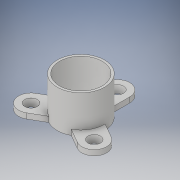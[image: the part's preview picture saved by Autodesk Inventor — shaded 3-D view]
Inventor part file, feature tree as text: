
AUTODESK INVENTOR PART (.ipt)
format: ipt  version: 2018 (Build 220112000, 112)  size: 190,976 bytes
history: native  units: in
note: dims shown in document units (in); Inventor stores cm internally (conversion verified against a paired STEP export)
features: sketch x5, extrude x4, plane x3, revolve x3, other x2, projected_geometry x1
ambient origin geometry x8: Origin, YZ Plane, XZ Plane, XY Plane, X Axis, Y Axis, Z Axis, Center Point
bodies: Solid1 (feature_tree)
feature tree (18):
  sketch  "Sketch1"  dims[d13=1.163in d14=0.0in d15=0.166in d16=0.0in]
  extrude  "Extrusion1"  Depth=0.166in TaperAngle=0.0deg
  extrude  "Extrusion2"  Depth=0.166in TaperAngle=0.0deg
  extrude  "Extrusion3"  TaperAngle=90.0deg  [1 undecoded]
  extrude  "Extrusion4"  TaperAngle=90.0deg  [1 undecoded]
  sketch  "Sketch2"  dims[d17=0.166in d18=0.0in d19=0.166in d20=0.0in]
  plane  "Work Plane1"
  sketch  "Sketch3"  dims[d23=-0.384in d24=90.0deg]
  other  "Work Axis1"
  revolve  "Revolution1"  Angle=90.0deg
  other  "Work Axis2"
  plane  "Work Plane2"
  revolve  "Revolution2"  [1 undecoded]
  plane  "Work Plane3"
  revolve  "Revolution3"  [1 undecoded]
  projected_geometry  "Projected Loop1"
  sketch  "Sketch4"  dims[d25=120.0deg d26=90.0deg]
  sketch  "Sketch5"  dims[d27=120.0deg d28=90.0deg]
note: 4 required parameter values undecoded (feature->parameter linkage not recoverable at this tier; creation-order binding heuristic only, values carry confidence <= 0.55)
